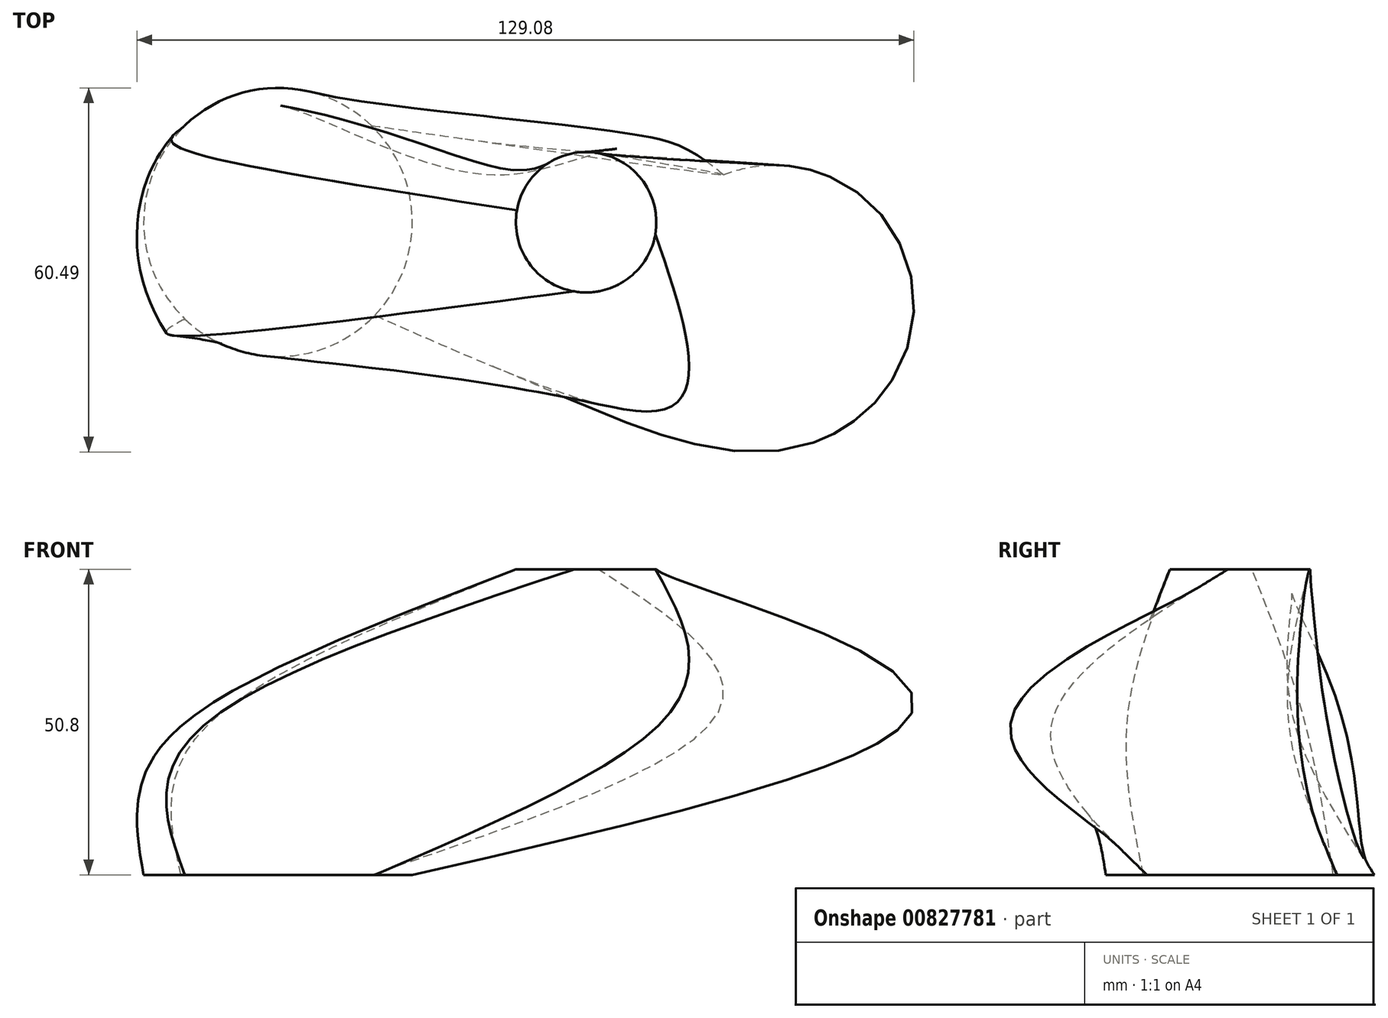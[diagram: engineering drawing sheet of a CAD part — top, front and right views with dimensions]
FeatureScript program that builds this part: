
annotation { "Feature Type Name" : "Feature", "Feature Type Description" : "" }
export const myFeature = defineFeature(function(context is Context, id is Id, definition is map)
    precondition{}
    {
        {
            var Q0;
            Q0=qCreatedBy(makeId("Top.planeOp"),FACE);
            cPlane(context, id + "F0", {"entities" : qUnion([Q0]), "cplaneType" : CPlaneType.OFFSET, "offset" : 25.4 * mm, "width" : 152.4 * mm, "height" : 152.4 * mm});
        }
        {
            var Q0;
            Q0=qCreatedBy(id+"F0.planeOp",FACE);
            cPlane(context, id + "F1", {"entities" : qUnion([Q0]), "cplaneType" : CPlaneType.OFFSET, "offset" : 25.4 * mm, "width" : 152.4 * mm, "height" : 152.4 * mm});
        }
        {
            var Q0;
            Q0=qCreatedBy(makeId("Top.planeOp"),FACE);
            var sketch = newSketch(context, id + "F2", { "sketchPlane" : qUnion([Q0])});
            skCircle(sketch, "E0", {"center": v(0, 0) * mm, "radius": 22.32 * mm});
            skSolve(sketch);
        }
        {
            var Q0;
            Q0=qCreatedBy(id+"F0.planeOp",FACE);
            var sketch = newSketch(context, id + "F3", { "sketchPlane" : qUnion([Q0])});
            skFitSpline(sketch, "E1", {"points": [v(-11.19, 10.76) * mm, v(11.7, 16.8) * mm, v(27.79, 9.16) * mm, v(58.47, 14.5) * mm, v(72.04, 8.09) * mm], "startDerivative": vector(94.69, 43.44) * mm, "endDerivative": vector(54.3, -45.84) * mm});
            skArc(sketch, "E2", {"start": v(-11.19, 10.76) * mm, "mid": v(-15.33, -4.44) * mm, "end": v(-11.19, -19.65) * mm});
            skArc(sketch, "E3", {"start": v(63.75, -31.2) * mm, "mid": v(26.38, -22.83) * mm, "end": v(-11.69, -18.76) * mm});
            skArc(sketch, "E4", {"start": v(63.75, -31.2) * mm, "mid": v(103.84, -19.15) * mm, "end": v(72.04, 8.09) * mm});
            skSolve(sketch);
        }
        {
            var Q0;
            Q0=qCreatedBy(id+"F1.planeOp",FACE);
            var sketch = newSketch(context, id + "F4", { "sketchPlane" : qUnion([Q0])});
            skCircle(sketch, "E5", {"center": v(51.18, 0) * mm, "radius": 11.66 * mm});
            skSolve(sketch);
        }
        {
            var Q0;
            Q0 = qSketchRegion(id + "F2", true);
            var Q1;
            Q1 = qSketchRegion(id + "F3", true);
            var Q2;
            Q2 = qSketchRegion(id + "F4", true);
            loft(context, id + "F5", {"sheetProfilesArray" : [{ "sheetProfileEntities" : qUnion([Q0]) }, { "sheetProfileEntities" : qUnion([Q1]) }, { "sheetProfileEntities" : qUnion([Q2]) }]});
        }
    });
